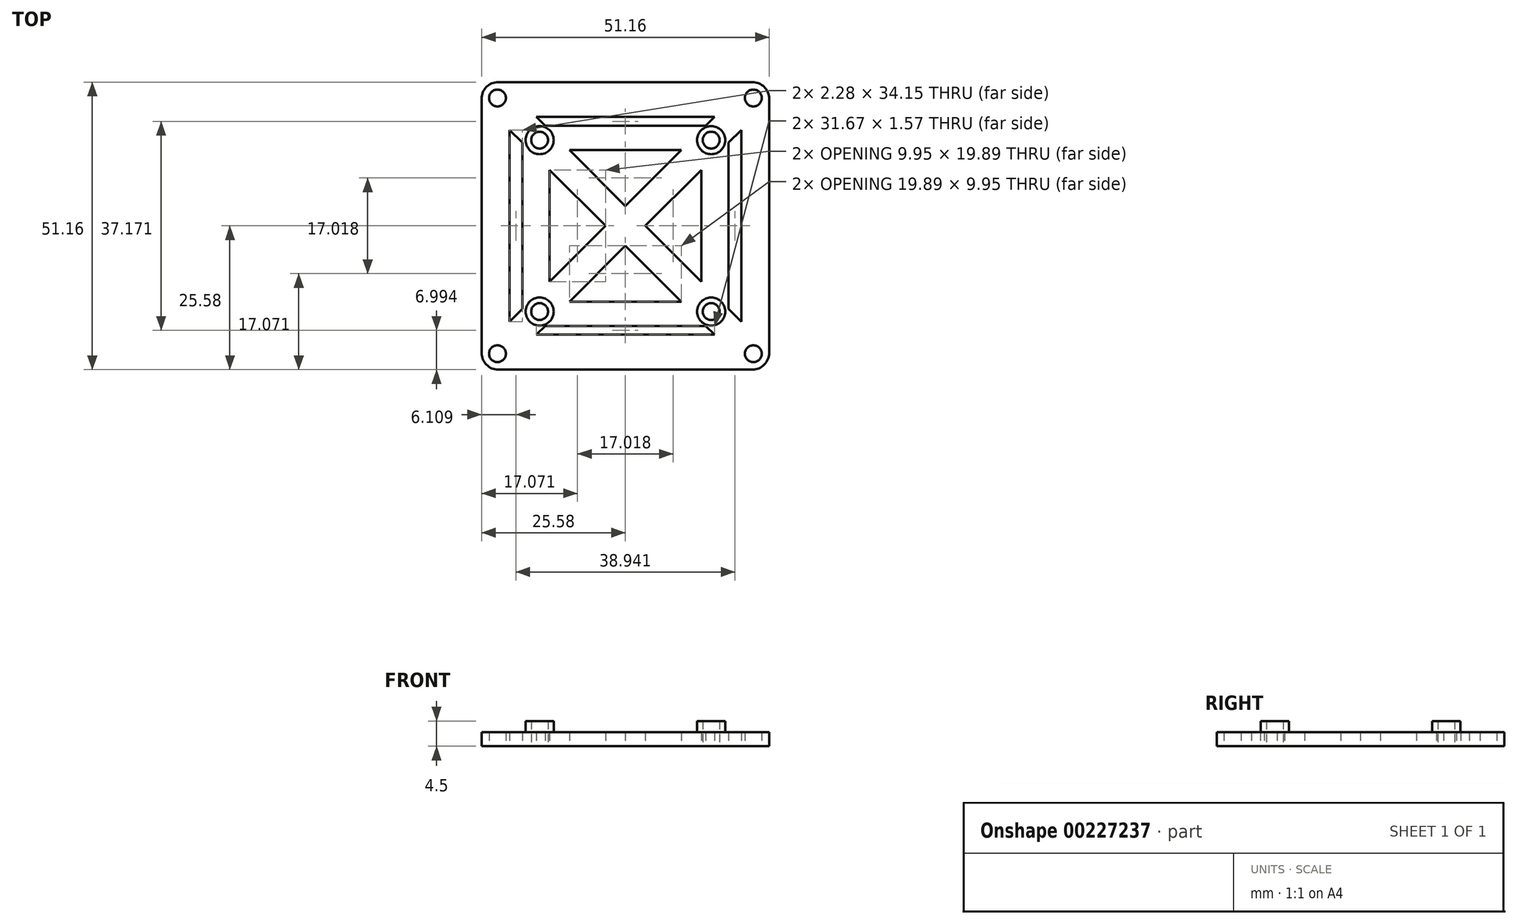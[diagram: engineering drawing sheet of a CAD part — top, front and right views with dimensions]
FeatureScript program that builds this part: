
annotation { "Feature Type Name" : "Feature", "Feature Type Description" : "" }
export const myFeature = defineFeature(function(context is Context, id is Id, definition is map)
    precondition{}
    {
        {
            var Q0;
            Q0=qCreatedBy(makeId("Top.planeOp"),FACE);
            var sketch = newSketch(context, id + "F0", { "sketchPlane" : qUnion([Q0])});
            skLineSegment(sketch, "E0.bottom", {"start": v(-22.75, 22.75) * mm, "end": v(22.75, 22.75) * mm, "construction": true});
            skLineSegment(sketch, "E0.top", {"start": v(-22.75, -22.75) * mm, "end": v(22.75, -22.75) * mm, "construction": true});
            skLineSegment(sketch, "E0.left", {"start": v(-22.75, 22.75) * mm, "end": v(-22.75, -22.75) * mm, "construction": true});
            skLineSegment(sketch, "E0.right", {"start": v(22.75, 22.75) * mm, "end": v(22.75, -22.75) * mm, "construction": true});
            skPoint(sketch, "E0.middle", {"position": v(0, 0) * mm});
            skLineSegment(sketch, "E1.bottom", {"start": v(-22.58, 25.58) * mm, "end": v(22.58, 25.58) * mm});
            skLineSegment(sketch, "E1.top", {"start": v(-22.58, -25.58) * mm, "end": v(22.58, -25.58) * mm});
            skLineSegment(sketch, "E1.left", {"start": v(-25.58, 22.58) * mm, "end": v(-25.58, -22.58) * mm});
            skLineSegment(sketch, "E1.right", {"start": v(25.58, 22.58) * mm, "end": v(25.58, -22.58) * mm});
            skCircle(sketch, "E2", {"center": v(-22.75, 22.75) * mm, "radius": 1.5 * mm});
            skCircle(sketch, "E3", {"center": v(22.75, 22.75) * mm, "radius": 1.5 * mm});
            skCircle(sketch, "E4", {"center": v(22.75, -22.75) * mm, "radius": 1.5 * mm});
            skCircle(sketch, "E5", {"center": v(-22.75, -22.75) * mm, "radius": 1.5 * mm});
            skLineSegment(sketch, "E6.bottom", {"start": v(-15.25, 15.25) * mm, "end": v(15.25, 15.25) * mm, "construction": true});
            skLineSegment(sketch, "E6.top", {"start": v(-15.25, -15.25) * mm, "end": v(15.25, -15.25) * mm, "construction": true});
            skLineSegment(sketch, "E6.left", {"start": v(-15.25, 15.25) * mm, "end": v(-15.25, -15.25) * mm, "construction": true});
            skLineSegment(sketch, "E6.right", {"start": v(15.25, 15.25) * mm, "end": v(15.25, -15.25) * mm, "construction": true});
            skCircle(sketch, "E7", {"center": v(-15.25, 15.25) * mm, "radius": 1.5 * mm});
            skCircle(sketch, "E8", {"center": v(15.25, 15.25) * mm, "radius": 1.5 * mm});
            skCircle(sketch, "E9", {"center": v(15.25, -15.25) * mm, "radius": 1.5 * mm});
            skCircle(sketch, "E10", {"center": v(-15.25, -15.25) * mm, "radius": 1.5 * mm});
            skLineSegment(sketch, "E11.bottom", {"start": v(13.48, -13.48) * mm, "end": v(-13.48, -13.48) * mm});
            skLineSegment(sketch, "E11.top", {"start": v(13.48, 13.48) * mm, "end": v(-13.48, 13.48) * mm});
            skLineSegment(sketch, "E11.left", {"start": v(13.48, -13.48) * mm, "end": v(13.48, 13.48) * mm});
            skLineSegment(sketch, "E11.right", {"start": v(-13.48, -13.48) * mm, "end": v(-13.48, 13.48) * mm});
            skLineSegment(sketch, "E12.bottom", {"start": v(-20.6, 19.37) * mm, "end": v(20.6, 19.37) * mm});
            skLineSegment(sketch, "E12.top", {"start": v(-20.6, -19.37) * mm, "end": v(20.6, -19.37) * mm});
            skLineSegment(sketch, "E12.left", {"start": v(-20.6, 19.37) * mm, "end": v(-20.6, -19.37) * mm});
            skLineSegment(sketch, "E12.right", {"start": v(20.6, 19.37) * mm, "end": v(20.6, -19.37) * mm});
            skLineSegment(sketch, "E13.bottom", {"start": v(-18.33, 17.8) * mm, "end": v(18.33, 17.8) * mm});
            skLineSegment(sketch, "E13.top", {"start": v(-18.33, -17.8) * mm, "end": v(18.33, -17.8) * mm});
            skLineSegment(sketch, "E13.left", {"start": v(-18.33, 17.8) * mm, "end": v(-18.33, -17.8) * mm});
            skLineSegment(sketch, "E13.right", {"start": v(18.33, 17.8) * mm, "end": v(18.33, -17.8) * mm});
            skLineSegment(sketch, "E14", {"start": v(-20.6, 17.07) * mm, "end": v(15.84, -19.37) * mm});
            skLineSegment(sketch, "E15", {"start": v(-15.84, 19.37) * mm, "end": v(20.6, -17.07) * mm});
            skLineSegment(sketch, "E16", {"start": v(0, 0) * mm, "end": v(-1.77, -1.77) * mm, "construction": true});
            skLineSegment(sketch, "E17", {"start": v(0, 0) * mm, "end": v(1.77, 1.77) * mm, "construction": true});
            skLineSegment(sketch, "E18.MirrorCS", {"start": v(15.84, 19.37) * mm, "end": v(-20.6, -17.07) * mm});
            skLineSegment(sketch, "E19.MirrorCS", {"start": v(20.6, 17.07) * mm, "end": v(-15.84, -19.37) * mm});
            skPoint(sketch, "E20.visualSharp", {"position": v(-25.58, 25.58) * mm});
            skArc(sketch, "E20.filletArc", {"start": v(-22.58, 25.58) * mm, "mid": v(-24.7, 24.7) * mm, "end": v(-25.58, 22.58) * mm});
            skPoint(sketch, "E21.visualSharp", {"position": v(25.58, 25.58) * mm});
            skArc(sketch, "E21.filletArc", {"start": v(25.58, 22.58) * mm, "mid": v(24.7, 24.7) * mm, "end": v(22.58, 25.58) * mm});
            skPoint(sketch, "E22.visualSharp", {"position": v(-25.58, -25.58) * mm});
            skArc(sketch, "E22.filletArc", {"start": v(-25.58, -22.58) * mm, "mid": v(-24.7, -24.7) * mm, "end": v(-22.58, -25.58) * mm});
            skPoint(sketch, "E23.visualSharp", {"position": v(25.58, -25.58) * mm});
            skArc(sketch, "E23.filletArc", {"start": v(22.58, -25.58) * mm, "mid": v(24.7, -24.7) * mm, "end": v(25.58, -22.58) * mm});
            skCircle(sketch, "E24", {"center": v(-15.25, 15.25) * mm, "radius": 2.5 * mm});
            skCircle(sketch, "E25.1.0", {"center": v(-15.25, -15.25) * mm, "radius": 2.5 * mm});
            skCircle(sketch, "E25.2.0", {"center": v(15.25, -15.25) * mm, "radius": 2.5 * mm});
            skCircle(sketch, "E25.3.0", {"center": v(15.25, 15.25) * mm, "radius": 2.5 * mm});
            skSolve(sketch);
        }
        {
            var Q0;
            {var subQ7=sQuery(id+"F0.wireOp",EDGE,"E12.left");var subQ8=sQuery(id+"F0.wireOp",EDGE,"E12.bottom");var subQ9=makeQuery(id+"F0.imprint","INTERSECT",VERTEX,{"derivedFrom":[subQ8,subQ7]});Q0=makeQuery(id+"F0.imprint","IMPRINT",FACE,{"disambiguationData":[TD([[makeQuery(id+"F0.imprint","IMPRINT",EDGE,{"disambiguationData":[TD([[subQ9,-1.0]])],"derivedFrom":subQ8}),-1.0]])]});}
            var Q1;
            Q1=makeQuery(id+"F0.imprint","IMPRINT",FACE,{"disambiguationData":[TD([[makeQuery(id+"F0.imprint","IMPRINT",EDGE,{"derivedFrom":sQuery(id+"F0.wireOp",EDGE,"E7")}),-1.0]])]});
            var Q2;
            {var subQ1=sQuery(id+"F0.wireOp",EDGE,"E11.top");var subQ6=sQuery(id+"F0.wireOp",EDGE,"E11.right");var subQ9=makeQuery(id+"F0.imprint","INTERSECT",VERTEX,{"derivedFrom":[subQ1,subQ6]});Q2=makeQuery(id+"F0.imprint","IMPRINT",FACE,{"disambiguationData":[TD([[makeQuery(id+"F0.imprint","IMPRINT",EDGE,{"disambiguationData":[TD([[subQ9,1.0]])],"derivedFrom":subQ1}),1.0]])]});}
            var Q3;
            {var subQ0=sQuery(id+"F0.wireOp",EDGE,"E18.MirrorCS");var subQ1=sQuery(id+"F0.wireOp",EDGE,"E11.top");var subQ2=makeQuery(id+"F0.imprint","INTERSECT",VERTEX,{"derivedFrom":[subQ1,subQ0]});Q3=makeQuery(id+"F0.imprint","IMPRINT",FACE,{"disambiguationData":[TD([[makeQuery(id+"F0.imprint","IMPRINT",EDGE,{"disambiguationData":[TD([[subQ2,-1.0]])],"derivedFrom":subQ1}),-1.0]])]});}
            var Q4;
            Q4=makeQuery(id+"F0.imprint","IMPRINT",FACE,{"disambiguationData":[TD([[makeQuery(id+"F0.imprint","IMPRINT",EDGE,{"derivedFrom":sQuery(id+"F0.wireOp",EDGE,"E8")}),-1.0]])]});
            var Q5;
            {var subQ0=sQuery(id+"F0.wireOp",EDGE,"E15");var subQ1=sQuery(id+"F0.wireOp",EDGE,"E11.left");var subQ2=makeQuery(id+"F0.imprint","INTERSECT",VERTEX,{"derivedFrom":[subQ1,subQ0]});Q5=makeQuery(id+"F0.imprint","IMPRINT",FACE,{"disambiguationData":[TD([[makeQuery(id+"F0.imprint","IMPRINT",EDGE,{"disambiguationData":[TD([[subQ2,-1.0]])],"derivedFrom":subQ1}),-1.0]])]});}
            var Q6;
            Q6=makeQuery(id+"F0.imprint","IMPRINT",FACE,{"disambiguationData":[TD([[makeQuery(id+"F0.imprint","IMPRINT",EDGE,{"derivedFrom":sQuery(id+"F0.wireOp",EDGE,"E9")}),-1.0]])]});
            var Q7;
            {var subQ1=sQuery(id+"F0.wireOp",EDGE,"E11.bottom");var subQ6=sQuery(id+"F0.wireOp",EDGE,"E11.left");var subQ9=makeQuery(id+"F0.imprint","INTERSECT",VERTEX,{"derivedFrom":[subQ1,subQ6]});Q7=makeQuery(id+"F0.imprint","IMPRINT",FACE,{"disambiguationData":[TD([[makeQuery(id+"F0.imprint","IMPRINT",EDGE,{"disambiguationData":[TD([[subQ9,-1.0]])],"derivedFrom":subQ1}),-1.0]])]});}
            var Q8;
            {var subQ0=sQuery(id+"F0.wireOp",EDGE,"E18.MirrorCS");var subQ1=sQuery(id+"F0.wireOp",EDGE,"E14");var subQ2=makeQuery(id+"F0.imprint","INTERSECT",VERTEX,{"derivedFrom":[subQ1,subQ0]});Q8=makeQuery(id+"F0.imprint","IMPRINT",FACE,{"disambiguationData":[TD([[makeQuery(id+"F0.imprint","IMPRINT",EDGE,{"disambiguationData":[TD([[subQ2,-1.0]])],"derivedFrom":subQ1}),1.0]])]});}
            var Q9;
            {var subQ1=sQuery(id+"F0.wireOp",EDGE,"E11.top");var subQ5=sQuery(id+"F0.wireOp",EDGE,"E11.left");var subQ6=makeQuery(id+"F0.imprint","INTERSECT",VERTEX,{"derivedFrom":[subQ1,subQ5]});Q9=makeQuery(id+"F0.imprint","IMPRINT",FACE,{"disambiguationData":[TD([[makeQuery(id+"F0.imprint","IMPRINT",EDGE,{"disambiguationData":[TD([[subQ6,-1.0]])],"derivedFrom":subQ1}),1.0]])]});}
            var Q10;
            {var subQ7=sQuery(id+"F0.wireOp",EDGE,"E12.bottom");var subQ9=sQuery(id+"F0.wireOp",EDGE,"E12.right");var subQ11=makeQuery(id+"F0.imprint","INTERSECT",VERTEX,{"derivedFrom":[subQ7,subQ9]});Q10=makeQuery(id+"F0.imprint","IMPRINT",FACE,{"disambiguationData":[TD([[makeQuery(id+"F0.imprint","IMPRINT",EDGE,{"disambiguationData":[TD([[subQ11,1.0]])],"derivedFrom":subQ7}),-1.0]])]});}
            var Q11;
            Q11=makeQuery(id+"F0.imprint","IMPRINT",FACE,{"disambiguationData":[TD([[makeQuery(id+"F0.imprint","IMPRINT",EDGE,{"derivedFrom":sQuery(id+"F0.wireOp",EDGE,"E1.bottom")}),-1.0]])]});
            var Q12;
            {var subQ5=sQuery(id+"F0.wireOp",EDGE,"E12.left");var subQ6=sQuery(id+"F0.wireOp",EDGE,"E12.top");var subQ7=makeQuery(id+"F0.imprint","INTERSECT",VERTEX,{"derivedFrom":[subQ6,subQ5]});Q12=makeQuery(id+"F0.imprint","IMPRINT",FACE,{"disambiguationData":[TD([[makeQuery(id+"F0.imprint","IMPRINT",EDGE,{"disambiguationData":[TD([[subQ7,-1.0]])],"derivedFrom":subQ6}),1.0]])]});}
            var Q13;
            Q13=makeQuery(id+"F0.imprint","IMPRINT",FACE,{"disambiguationData":[TD([[makeQuery(id+"F0.imprint","IMPRINT",EDGE,{"derivedFrom":sQuery(id+"F0.wireOp",EDGE,"E10")}),-1.0]])]});
            var Q14;
            {var subQ1=sQuery(id+"F0.wireOp",EDGE,"E11.right");var subQ6=sQuery(id+"F0.wireOp",EDGE,"E11.bottom");var subQ9=makeQuery(id+"F0.imprint","INTERSECT",VERTEX,{"derivedFrom":[subQ6,subQ1]});Q14=makeQuery(id+"F0.imprint","IMPRINT",FACE,{"disambiguationData":[TD([[makeQuery(id+"F0.imprint","IMPRINT",EDGE,{"disambiguationData":[TD([[subQ9,1.0]])],"derivedFrom":subQ6}),-1.0]])]});}
            var Q15;
            {var subQ0=sQuery(id+"F0.wireOp",EDGE,"E14");var subQ1=sQuery(id+"F0.wireOp",EDGE,"E11.bottom");var subQ2=makeQuery(id+"F0.imprint","INTERSECT",VERTEX,{"derivedFrom":[subQ1,subQ0]});Q15=makeQuery(id+"F0.imprint","IMPRINT",FACE,{"disambiguationData":[TD([[makeQuery(id+"F0.imprint","IMPRINT",EDGE,{"disambiguationData":[TD([[subQ2,-1.0]])],"derivedFrom":subQ1}),1.0]])]});}
            var Q16;
            {var subQ0=sQuery(id+"F0.wireOp",EDGE,"E18.MirrorCS");var subQ1=sQuery(id+"F0.wireOp",EDGE,"E11.right");var subQ2=makeQuery(id+"F0.imprint","INTERSECT",VERTEX,{"derivedFrom":[subQ1,subQ0]});Q16=makeQuery(id+"F0.imprint","IMPRINT",FACE,{"disambiguationData":[TD([[makeQuery(id+"F0.imprint","IMPRINT",EDGE,{"disambiguationData":[TD([[subQ2,-1.0]])],"derivedFrom":subQ1}),1.0]])]});}
            var Q17;
            {var subQ5=sQuery(id+"F0.wireOp",EDGE,"E12.right");var subQ6=sQuery(id+"F0.wireOp",EDGE,"E12.top");var subQ7=makeQuery(id+"F0.imprint","INTERSECT",VERTEX,{"derivedFrom":[subQ6,subQ5]});Q17=makeQuery(id+"F0.imprint","IMPRINT",FACE,{"disambiguationData":[TD([[makeQuery(id+"F0.imprint","IMPRINT",EDGE,{"disambiguationData":[TD([[subQ7,1.0]])],"derivedFrom":subQ6}),1.0]])]});}
            var Q18;
            {var subQ1=sQuery(id+"F0.wireOp",EDGE,"E13.bottom");var subQ5=sQuery(id+"F0.wireOp",EDGE,"E13.left");var subQ6=makeQuery(id+"F0.imprint","INTERSECT",VERTEX,{"derivedFrom":[subQ1,subQ5]});Q18=makeQuery(id+"F0.imprint","IMPRINT",FACE,{"disambiguationData":[TD([[makeQuery(id+"F0.imprint","IMPRINT",EDGE,{"disambiguationData":[TD([[subQ6,-1.0]])],"derivedFrom":subQ1}),-1.0]])]});}
            var Q19;
            {var subQ1=sQuery(id+"F0.wireOp",EDGE,"E11.top");var subQ3=sQuery(id+"F0.wireOp",EDGE,"E15");var subQ4=makeQuery(id+"F0.imprint","INTERSECT",VERTEX,{"derivedFrom":[subQ1,subQ3]});Q19=makeQuery(id+"F0.imprint","IMPRINT",FACE,{"disambiguationData":[TD([[makeQuery(id+"F0.imprint","IMPRINT",EDGE,{"disambiguationData":[TD([[subQ4,1.0]])],"derivedFrom":subQ3}),-1.0]])]});}
            var Q20;
            {var subQ1=sQuery(id+"F0.wireOp",EDGE,"E11.right");var subQ3=sQuery(id+"F0.wireOp",EDGE,"E14");var subQ4=makeQuery(id+"F0.imprint","INTERSECT",VERTEX,{"derivedFrom":[subQ1,subQ3]});Q20=makeQuery(id+"F0.imprint","IMPRINT",FACE,{"disambiguationData":[TD([[makeQuery(id+"F0.imprint","IMPRINT",EDGE,{"disambiguationData":[TD([[subQ4,1.0]])],"derivedFrom":subQ3}),1.0]])]});}
            var Q21;
            {var subQ1=sQuery(id+"F0.wireOp",EDGE,"E11.top");var subQ3=sQuery(id+"F0.wireOp",EDGE,"E18.MirrorCS");var subQ4=makeQuery(id+"F0.imprint","INTERSECT",VERTEX,{"derivedFrom":[subQ1,subQ3]});Q21=makeQuery(id+"F0.imprint","IMPRINT",FACE,{"disambiguationData":[TD([[makeQuery(id+"F0.imprint","IMPRINT",EDGE,{"disambiguationData":[TD([[subQ4,1.0]])],"derivedFrom":subQ3}),1.0]])]});}
            var Q22;
            {var subQ1=sQuery(id+"F0.wireOp",EDGE,"E11.left");var subQ3=sQuery(id+"F0.wireOp",EDGE,"E19.MirrorCS");var subQ4=makeQuery(id+"F0.imprint","INTERSECT",VERTEX,{"derivedFrom":[subQ1,subQ3]});Q22=makeQuery(id+"F0.imprint","IMPRINT",FACE,{"disambiguationData":[TD([[makeQuery(id+"F0.imprint","IMPRINT",EDGE,{"disambiguationData":[TD([[subQ4,1.0]])],"derivedFrom":subQ3}),-1.0]])]});}
            var Q23;
            {var subQ1=sQuery(id+"F0.wireOp",EDGE,"E13.right");var subQ6=sQuery(id+"F0.wireOp",EDGE,"E13.bottom");var subQ9=makeQuery(id+"F0.imprint","INTERSECT",VERTEX,{"derivedFrom":[subQ6,subQ1]});Q23=makeQuery(id+"F0.imprint","IMPRINT",FACE,{"disambiguationData":[TD([[makeQuery(id+"F0.imprint","IMPRINT",EDGE,{"disambiguationData":[TD([[subQ9,1.0]])],"derivedFrom":subQ6}),-1.0]])]});}
            var Q24;
            {var subQ1=sQuery(id+"F0.wireOp",EDGE,"E13.right");var subQ6=sQuery(id+"F0.wireOp",EDGE,"E13.top");var subQ9=makeQuery(id+"F0.imprint","INTERSECT",VERTEX,{"derivedFrom":[subQ6,subQ1]});Q24=makeQuery(id+"F0.imprint","IMPRINT",FACE,{"disambiguationData":[TD([[makeQuery(id+"F0.imprint","IMPRINT",EDGE,{"disambiguationData":[TD([[subQ9,1.0]])],"derivedFrom":subQ6}),1.0]])]});}
            var Q25;
            {var subQ1=sQuery(id+"F0.wireOp",EDGE,"E11.left");var subQ3=sQuery(id+"F0.wireOp",EDGE,"E15");var subQ4=makeQuery(id+"F0.imprint","INTERSECT",VERTEX,{"derivedFrom":[subQ1,subQ3]});Q25=makeQuery(id+"F0.imprint","IMPRINT",FACE,{"disambiguationData":[TD([[makeQuery(id+"F0.imprint","IMPRINT",EDGE,{"disambiguationData":[TD([[subQ4,-1.0]])],"derivedFrom":subQ3}),-1.0]])]});}
            var Q26;
            {var subQ1=sQuery(id+"F0.wireOp",EDGE,"E11.bottom");var subQ3=sQuery(id+"F0.wireOp",EDGE,"E14");var subQ4=makeQuery(id+"F0.imprint","INTERSECT",VERTEX,{"derivedFrom":[subQ1,subQ3]});Q26=makeQuery(id+"F0.imprint","IMPRINT",FACE,{"disambiguationData":[TD([[makeQuery(id+"F0.imprint","IMPRINT",EDGE,{"disambiguationData":[TD([[subQ4,-1.0]])],"derivedFrom":subQ3}),1.0]])]});}
            var Q27;
            {var subQ1=sQuery(id+"F0.wireOp",EDGE,"E11.bottom");var subQ3=sQuery(id+"F0.wireOp",EDGE,"E19.MirrorCS");var subQ4=makeQuery(id+"F0.imprint","INTERSECT",VERTEX,{"derivedFrom":[subQ1,subQ3]});Q27=makeQuery(id+"F0.imprint","IMPRINT",FACE,{"disambiguationData":[TD([[makeQuery(id+"F0.imprint","IMPRINT",EDGE,{"disambiguationData":[TD([[subQ4,-1.0]])],"derivedFrom":subQ3}),-1.0]])]});}
            var Q28;
            {var subQ1=sQuery(id+"F0.wireOp",EDGE,"E11.right");var subQ3=sQuery(id+"F0.wireOp",EDGE,"E18.MirrorCS");var subQ4=makeQuery(id+"F0.imprint","INTERSECT",VERTEX,{"derivedFrom":[subQ1,subQ3]});Q28=makeQuery(id+"F0.imprint","IMPRINT",FACE,{"disambiguationData":[TD([[makeQuery(id+"F0.imprint","IMPRINT",EDGE,{"disambiguationData":[TD([[subQ4,-1.0]])],"derivedFrom":subQ3}),1.0]])]});}
            var Q29;
            {var subQ1=sQuery(id+"F0.wireOp",EDGE,"E13.top");var subQ6=sQuery(id+"F0.wireOp",EDGE,"E13.left");var subQ9=makeQuery(id+"F0.imprint","INTERSECT",VERTEX,{"derivedFrom":[subQ1,subQ6]});Q29=makeQuery(id+"F0.imprint","IMPRINT",FACE,{"disambiguationData":[TD([[makeQuery(id+"F0.imprint","IMPRINT",EDGE,{"disambiguationData":[TD([[subQ9,-1.0]])],"derivedFrom":subQ1}),1.0]])]});}
            extrude(context, id + "F1", {"entities" : qUnion([Q0, Q1, Q2, Q3, Q4, Q5, Q6, Q7, Q8, Q9, Q10, Q11, Q12, Q13, Q14, Q15, Q16, Q17, Q18, Q19, Q20, Q21, Q22, Q23, Q24, Q25, Q26, Q27, Q28, Q29]), "depth" : 2.5 * mm});
        }
        {
            var Q0;
            Q0=makeQuery(id+"F0.imprint","IMPRINT",FACE,{"disambiguationData":[TD([[makeQuery(id+"F0.imprint","IMPRINT",EDGE,{"derivedFrom":sQuery(id+"F0.wireOp",EDGE,"E10")}),-1.0]])]});
            var Q1;
            Q1=makeQuery(id+"F0.imprint","IMPRINT",FACE,{"disambiguationData":[TD([[makeQuery(id+"F0.imprint","IMPRINT",EDGE,{"derivedFrom":sQuery(id+"F0.wireOp",EDGE,"E7")}),-1.0]])]});
            var Q2;
            Q2=makeQuery(id+"F0.imprint","IMPRINT",FACE,{"disambiguationData":[TD([[makeQuery(id+"F0.imprint","IMPRINT",EDGE,{"derivedFrom":sQuery(id+"F0.wireOp",EDGE,"E9")}),-1.0]])]});
            var Q3;
            Q3=makeQuery(id+"F0.imprint","IMPRINT",FACE,{"disambiguationData":[TD([[makeQuery(id+"F0.imprint","IMPRINT",EDGE,{"derivedFrom":sQuery(id+"F0.wireOp",EDGE,"E8")}),-1.0]])]});
            extrude(context, id + "F2", {"entities" : qUnion([Q0, Q1, Q2, Q3]), "operationType" : NewBodyOperationType.ADD, "depth" : 4.5 * mm});
        }
    });
